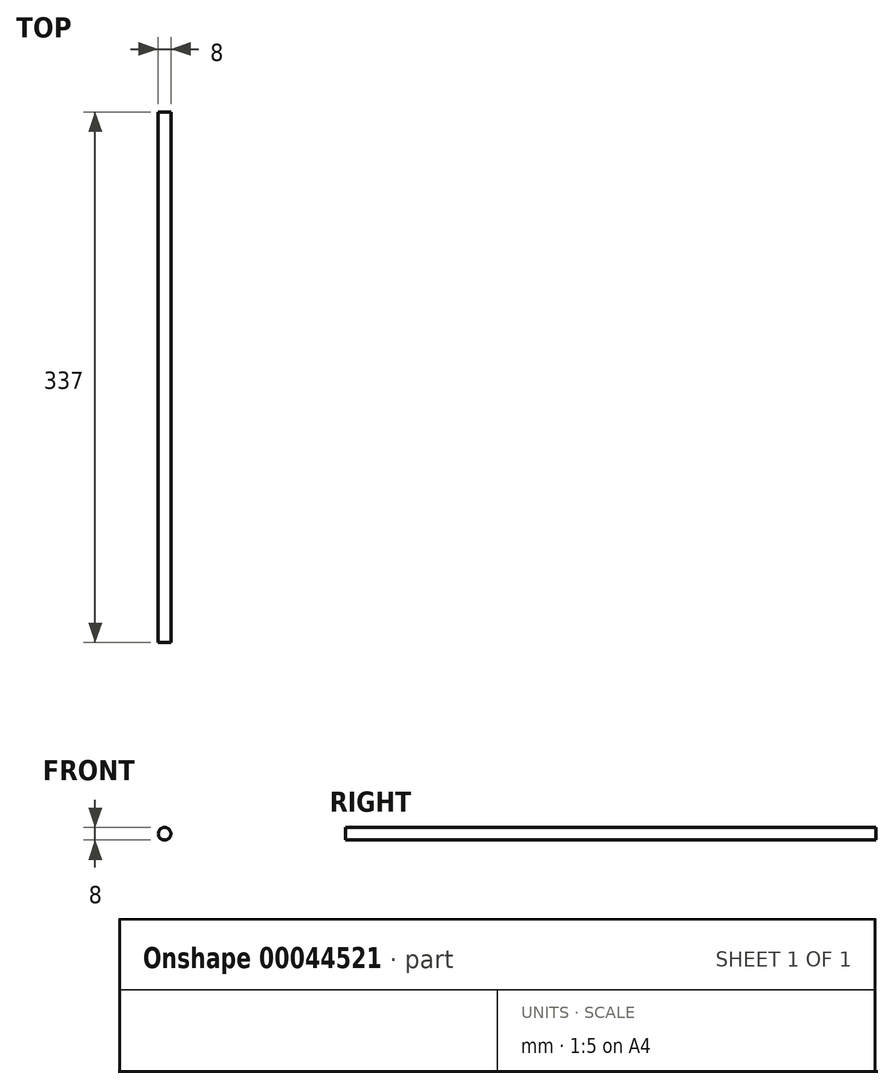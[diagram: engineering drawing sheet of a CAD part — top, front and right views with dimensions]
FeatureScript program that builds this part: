
annotation { "Feature Type Name" : "Feature", "Feature Type Description" : "" }
export const myFeature = defineFeature(function(context is Context, id is Id, definition is map)
    precondition{}
    {
        {
            var Q0;
            Q0=qCreatedBy(makeId("Front.planeOp"),FACE);
            var sketch = newSketch(context, id + "F0", { "sketchPlane" : qUnion([Q0])});
            skCircle(sketch, "E0", {"center": v(0, 0) * mm, "radius": 4 * mm});
            skSolve(sketch);
        }
        {
            var Q0;
            Q0 = qSketchRegion(id + "F0", true);
            extrude(context, id + "F1", {"entities" : qUnion([Q0]), "depth" : 337 * mm});
        }
    });
